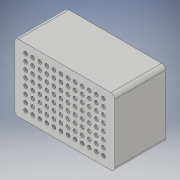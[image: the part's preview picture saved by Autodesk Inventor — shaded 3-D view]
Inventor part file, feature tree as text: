
AUTODESK INVENTOR PART (.ipt)
format: ipt  version: 2019.4 (Build 234330000, 330)  size: 245,760 bytes
history: native  units: mm
features: reference x5, extrude x3, sketch x2, other x2, fillet x1, pattern_linear x1, projected_geometry x1
ambient origin geometry x8: Origin, YZ Plane, XZ Plane, XY Plane, X Axis, Y Axis, Z Axis, Center Point
bodies: Solid1 (feature_tree)
feature tree (15):
  extrude  "Extrusion1"  Depth=5.0mm
  fillet  "Fillet1"  Radius=2.0mm
  extrude  "Extrusion2"  Depth=127.76mm
  extrude  "Extrusion3"  Depth=85.48mm
  pattern_linear  "Rectangular Pattern1"  Spacing1=4.75mm  [1 undecoded]
  sketch  "Sketch1"  dims[d0=2.0mm d1=0.0mm d2=5.0mm d13=2.0mm d14=0.0mm]
  reference  "Reference1"
  reference  "Reference2"
  reference  "Reference3"
  reference  "Reference4"
  reference  "Reference5"
  sketch  "Sketch2"  dims[d28=62.49mm d29=0.0mm d30=127.76mm d31=85.48mm d35=4.75mm d36=14.38mm d37=11.24mm d38=120.0mm d40=9.0mm d41=80.0mm d43=9.0mm]
  projected_geometry  "Projected Loop2"
  other  "Assembly1"
  other  "00_MTP_96-welplate:1"
note: 1 required parameter value undecoded (feature->parameter linkage not recoverable at this tier; creation-order binding heuristic only, values carry confidence <= 0.55)
